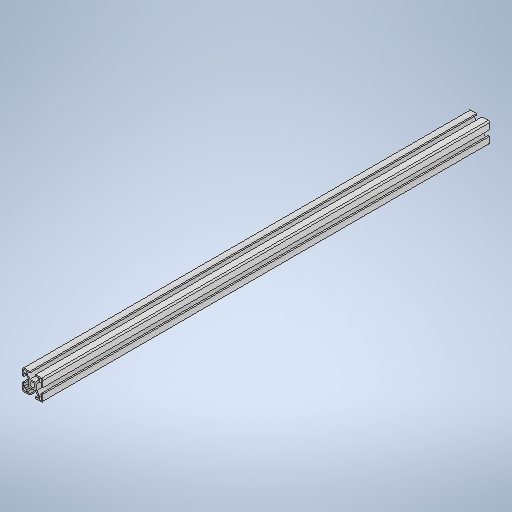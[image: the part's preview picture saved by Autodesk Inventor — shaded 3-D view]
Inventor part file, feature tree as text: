
AUTODESK INVENTOR PART (.ipt)
format: ipt  version: 2025 (Build 290162000, 162)  size: 315,392 bytes
history: native  units: in
note: dims shown in document units (in); Inventor stores cm internally (conversion verified against a paired STEP export)
features: extrude x1, sketch x1
ambient origin geometry x8: Origin, YZ Plane, XZ Plane, XY Plane, X Axis, Y Axis, Z Axis, Center Point
bodies: Solid1 (feature_tree)
feature tree (2):
  extrude  "Extrusion1"  Depth=25.5906in
  sketch  "Sketch1"  dims[d6=25.5906in d7=0.0in d8=0.1969in d9=0.0344in]
